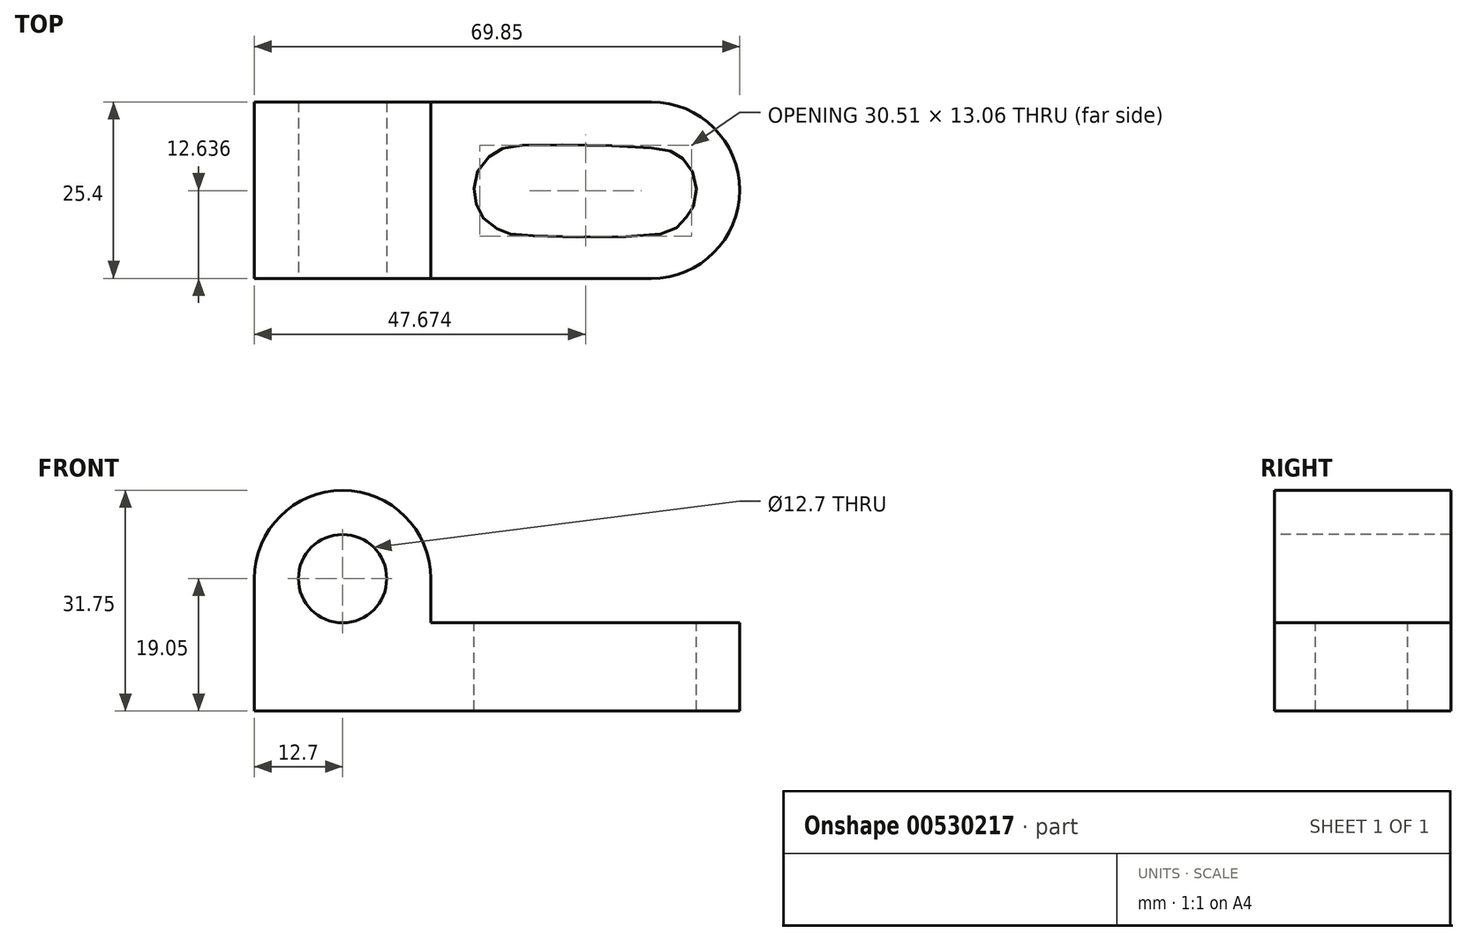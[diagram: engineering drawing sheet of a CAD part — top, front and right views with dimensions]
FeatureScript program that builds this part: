
annotation { "Feature Type Name" : "Feature", "Feature Type Description" : "" }
export const myFeature = defineFeature(function(context is Context, id is Id, definition is map)
    precondition{}
    {
        {
            var Q0;
            Q0=qCreatedBy(makeId("Front.planeOp"),FACE);
            var sketch = newSketch(context, id + "F0", { "sketchPlane" : qUnion([Q0])});
            skLineSegment(sketch, "E0", {"start": v(0, 0) * mm, "end": v(-57.15, 0) * mm});
            skLineSegment(sketch, "E1", {"start": v(-57.15, 0) * mm, "end": v(-57.15, 12.7) * mm});
            skLineSegment(sketch, "E2", {"start": v(-57.15, 12.7) * mm, "end": v(0, 12.7) * mm});
            skLineSegment(sketch, "E3", {"start": v(0, 12.7) * mm, "end": v(0, 0) * mm});
            skSolve(sketch);
        }
        {
            var Q0;
            Q0=makeQuery(id+"F0.imprint","IMPRINT",FACE,{"disambiguationData":[TD([[makeQuery(id+"F0.imprint","IMPRINT",EDGE,{"derivedFrom":sQuery(id+"F0.wireOp",EDGE,"E0")}),-1.0]])]});
            extrude(context, id + "F1", {"entities" : qUnion([Q0]), "depth" : 25.4 * mm, "offsetDistance" : 25.4 * mm});
        }
        {
            var Q0;
            Q0=makeQuery(id+"F1.opExtrude","SWEPT_FACE",FACE,{"disambiguationData":[OSD([sQuery(id+"F0.wireOp",EDGE,"E2")])]});
            var sketch = newSketch(context, id + "F2", { "sketchPlane" : qUnion([Q0])});
            skArc(sketch, "E4", {"start": v(0, -25.4) * mm, "mid": v(12.7, -12.7) * mm, "end": v(0, 0) * mm});
            skSolve(sketch);
        }
        {
            var Q0;
            Q0=makeQuery(id+"F2.imprint","IMPRINT",FACE,{"disambiguationData":[TD([[makeQuery(id+"F2.imprint","IMPRINT",EDGE,{"derivedFrom":sQuery(id+"F2.wireOp",EDGE,"E4")}),1.0]])]});
            extrude(context, id + "F3", {"entities" : qUnion([Q0]), "operationType" : NewBodyOperationType.ADD, "oppositeDirection" : true, "depth" : 12.7 * mm, "offsetDistance" : 25.4 * mm});
        }
        {
            var Q0;
            {var subQ0=sQuery(id+"F0.wireOp",EDGE,"E2");Q0=makeQuery(id+"F3.boolean.opBoolean","MERGE",FACE,{"derivedFrom":[makeQuery(id+"F1.opExtrude","SWEPT_FACE",FACE,{"disambiguationData":[OSD([subQ0])]}),makeQuery(id+"F3.opExtrude","CAP_FACE",FACE,{"disambiguationData":[OSD([subQ0,sQuery(id+"F0.wireOp",EDGE,"E3"),sQuery(id+"F2.wireOp",EDGE,"E4")])],"isStart":true})]});}
            var sketch = newSketch(context, id + "F4", { "sketchPlane" : qUnion([Q0])});
            skLineSegment(sketch, "E5", {"start": v(-57.15, 0) * mm, "end": v(-31.75, 0) * mm});
            skLineSegment(sketch, "E6", {"start": v(-31.75, 0) * mm, "end": v(-31.75, -25.4) * mm});
            skLineSegment(sketch, "E7", {"start": v(-31.75, -25.4) * mm, "end": v(-57.15, -25.4) * mm});
            skLineSegment(sketch, "E8", {"start": v(-57.15, -25.4) * mm, "end": v(-57.15, 0) * mm});
            skSolve(sketch);
        }
        {
            var Q0;
            Q0=makeQuery(id+"F4.imprint","IMPRINT",FACE,{"disambiguationData":[TD([[makeQuery(id+"F4.imprint","IMPRINT",EDGE,{"derivedFrom":sQuery(id+"F4.wireOp",EDGE,"E5")}),-1.0]])]});
            extrude(context, id + "F5", {"entities" : qUnion([Q0]), "operationType" : NewBodyOperationType.ADD, "depth" : 6.35 * mm, "offsetDistance" : 25.4 * mm});
        }
        {
            var Q0;
            Q0=makeQuery(id+"F5.boolean.opBoolean","MERGE",FACE,{"derivedFrom":[makeQuery(id+"F1.opExtrude","CAP_FACE",FACE,{"disambiguationData":[OSD([sQuery(id+"F0.wireOp",EDGE,"E0"),sQuery(id+"F0.wireOp",EDGE,"E1"),sQuery(id+"F0.wireOp",EDGE,"E2"),sQuery(id+"F0.wireOp",EDGE,"E3")])],"isStart":false}),makeQuery(id+"F5.opExtrude","SWEPT_FACE",FACE,{"disambiguationData":[OSD([sQuery(id+"F4.wireOp",EDGE,"E7")])]})]});
            var sketch = newSketch(context, id + "F6", { "sketchPlane" : qUnion([Q0])});
            skArc(sketch, "E9", {"start": v(-31.75, 19.05) * mm, "mid": v(-44.45, 31.75) * mm, "end": v(-57.15, 19.05) * mm});
            skSolve(sketch);
        }
        {
            var Q0;
            Q0 = qSketchRegion(id + "F6", true);
            var Q1;
            Q1=makeQuery(id+"F6.imprint","IMPRINT",FACE,{"disambiguationData":[TD([[makeQuery(id+"F6.imprint","IMPRINT",EDGE,{"derivedFrom":sQuery(id+"F6.wireOp",EDGE,"E9")}),1.0]])]});
            extrude(context, id + "F7", {"entities" : qUnion([Q0, Q1]), "operationType" : NewBodyOperationType.ADD, "oppositeDirection" : true, "depth" : 25.4 * mm, "offsetDistance" : 25.4 * mm});
        }
        {
            var Q0;
            {var subQ0=sQuery(id+"F4.wireOp",EDGE,"E7");Q0=makeQuery(id+"F7.boolean.opBoolean","MERGE",FACE,{"derivedFrom":[makeQuery(id+"F5.boolean.opBoolean","MERGE",FACE,{"derivedFrom":[makeQuery(id+"F1.opExtrude","CAP_FACE",FACE,{"disambiguationData":[OSD([sQuery(id+"F0.wireOp",EDGE,"E0"),sQuery(id+"F0.wireOp",EDGE,"E1"),sQuery(id+"F0.wireOp",EDGE,"E2"),sQuery(id+"F0.wireOp",EDGE,"E3")])],"isStart":false}),makeQuery(id+"F5.opExtrude","SWEPT_FACE",FACE,{"disambiguationData":[OSD([subQ0])]})]}),makeQuery(id+"F7.opExtrude","CAP_FACE",FACE,{"disambiguationData":[OSD([subQ0,sQuery(id+"F6.wireOp",EDGE,"E9")])],"isStart":true})]});}
            var sketch = newSketch(context, id + "F8", { "sketchPlane" : qUnion([Q0])});
            skCircle(sketch, "E10", {"center": v(-44.45, 19.05) * mm, "radius": 6.35 * mm});
            skSolve(sketch);
        }
        {
            var Q0;
            Q0=makeQuery(id+"F8.imprint","IMPRINT",FACE,{"disambiguationData":[TD([[makeQuery(id+"F8.imprint","IMPRINT",EDGE,{"derivedFrom":sQuery(id+"F8.wireOp",EDGE,"E10")}),1.0]])]});
            extrude(context, id + "F9", {"entities" : qUnion([Q0]), "operationType" : NewBodyOperationType.REMOVE, "oppositeDirection" : true, "depth" : 25.4 * mm, "offsetDistance" : 25.4 * mm});
        }
        {
            var Q0;
            {var subQ0=sQuery(id+"F0.wireOp",EDGE,"E2");Q0=makeQuery(id+"F3.boolean.opBoolean","MERGE",FACE,{"derivedFrom":[makeQuery(id+"F1.opExtrude","SWEPT_FACE",FACE,{"disambiguationData":[OSD([subQ0])]}),makeQuery(id+"F3.opExtrude","CAP_FACE",FACE,{"disambiguationData":[OSD([subQ0,sQuery(id+"F0.wireOp",EDGE,"E3"),sQuery(id+"F2.wireOp",EDGE,"E4")])],"isStart":true})]});}
            var sketch = newSketch(context, id + "F10", { "sketchPlane" : qUnion([Q0])});
            skArc(sketch, "E11", {"start": v(0, -19.05) * mm, "mid": v(6.35, -12.7) * mm, "end": v(0, -6.35) * mm});
            skSolve(sketch);
        }
        {
            var Q0;
            Q0=makeQuery(id+"F10.imprint","IMPRINT",FACE,{"disambiguationData":[TD([[makeQuery(id+"F10.imprint","IMPRINT",EDGE,{"derivedFrom":makeQuery(id+"F3.opExtrude","CAP_EDGE",EDGE,{"disambiguationData":[OSD([sQuery(id+"F2.wireOp",EDGE,"E4")])],"isStart":true})}),1.0]])]});
            var sketch = newSketch(context, id + "F11", { "sketchPlane" : qUnion([Q0])});
            skSolve(sketch);
        }
        {
            var Q0;
            Q0=makeQuery(id+"F11.imprint","IMPRINT",FACE,{"disambiguationData":[TD([[makeQuery(id+"F11.imprint","IMPRINT",EDGE,{"derivedFrom":makeQuery(id+"F10.imprint","IMPRINT",EDGE,{"derivedFrom":makeQuery(id+"F3.opExtrude","CAP_EDGE",EDGE,{"disambiguationData":[OSD([sQuery(id+"F2.wireOp",EDGE,"E4")])],"isStart":true})})}),1.0]])]});
            var sketch = newSketch(context, id + "F12", { "sketchPlane" : qUnion([Q0])});
            skFitSpline(sketch, "E12", {"points": [v(0, -6.6) * mm, v(-19.03, -6.28) * mm, v(-22.01, -7) * mm, v(-24.58, -9.16) * mm, v(-25.5, -12.3) * mm, v(-25.15, -14.87) * mm, v(-23.86, -17.13) * mm, v(-21.24, -18.72) * mm, v(-18.88, -19.19) * mm, v(0, -19.19) * mm, v(3.69, -18.06) * mm, v(5.13, -16.46) * mm, v(6.1, -14.92) * mm, v(6.41, -11.58) * mm, v(5.13, -8.8) * mm, v(3.28, -7.31) * mm, v(0, -6.6) * mm]});
            skSolve(sketch);
        }
        {
            var Q0;
            Q0 = qSketchRegion(id + "F12", true);
            extrude(context, id + "F13", {"entities" : qUnion([Q0]), "operationType" : NewBodyOperationType.REMOVE, "oppositeDirection" : true, "depth" : 25.4 * mm, "offsetDistance" : 25.4 * mm});
        }
    });
